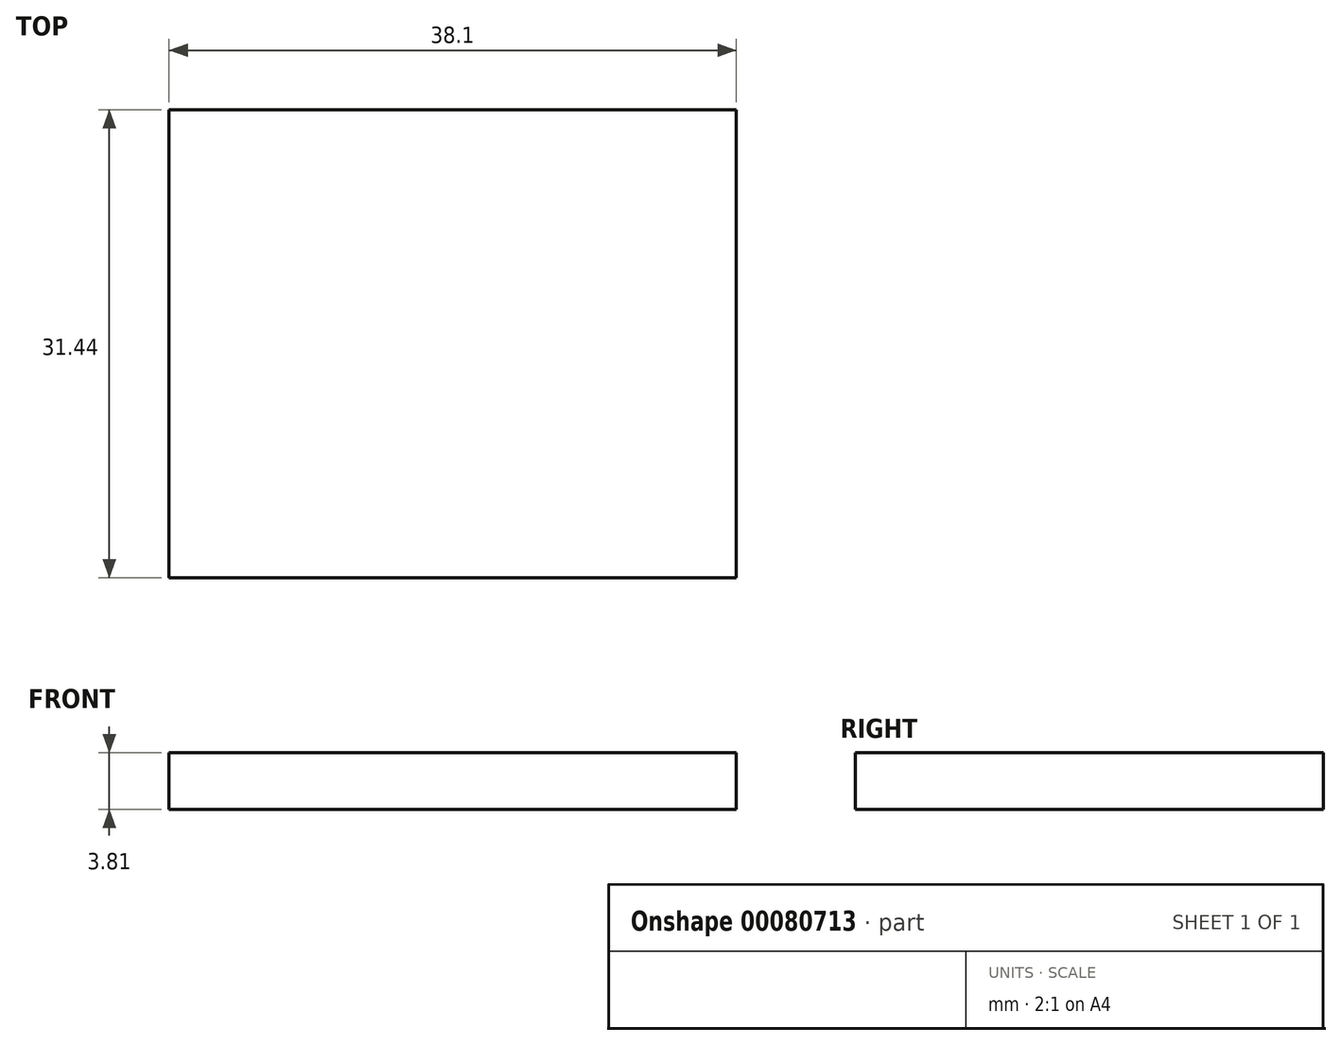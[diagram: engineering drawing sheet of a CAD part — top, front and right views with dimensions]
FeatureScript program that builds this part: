
annotation { "Feature Type Name" : "Feature", "Feature Type Description" : "" }
export const myFeature = defineFeature(function(context is Context, id is Id, definition is map)
    precondition{}
    {
        {
            var Q0;
            Q0=qCreatedBy(makeId("Top.planeOp"),FACE);
            var sketch = newSketch(context, id + "F0", { "sketchPlane" : qUnion([Q0])});
            skLineSegment(sketch, "E0.bottom", {"start": v(19.05, -15.72) * mm, "end": v(-19.05, -15.72) * mm});
            skLineSegment(sketch, "E0.top", {"start": v(19.05, 15.72) * mm, "end": v(-19.05, 15.72) * mm});
            skLineSegment(sketch, "E0.left", {"start": v(19.05, -15.72) * mm, "end": v(19.05, 15.72) * mm});
            skLineSegment(sketch, "E0.right", {"start": v(-19.05, -15.72) * mm, "end": v(-19.05, 15.72) * mm});
            skPoint(sketch, "E0.middle", {"position": v(0, 0) * mm});
            skSolve(sketch);
        }
        {
            var Q0;
            Q0=makeQuery(id+"F0.imprint","IMPRINT",FACE,{"disambiguationData":[TD([[makeQuery(id+"F0.imprint","IMPRINT",EDGE,{"derivedFrom":sQuery(id+"F0.wireOp",EDGE,"E0.bottom")}),-1.0]])]});
            extrude(context, id + "F1", {"entities" : qUnion([Q0]), "depth" : 3.8 * mm});
        }
    });
